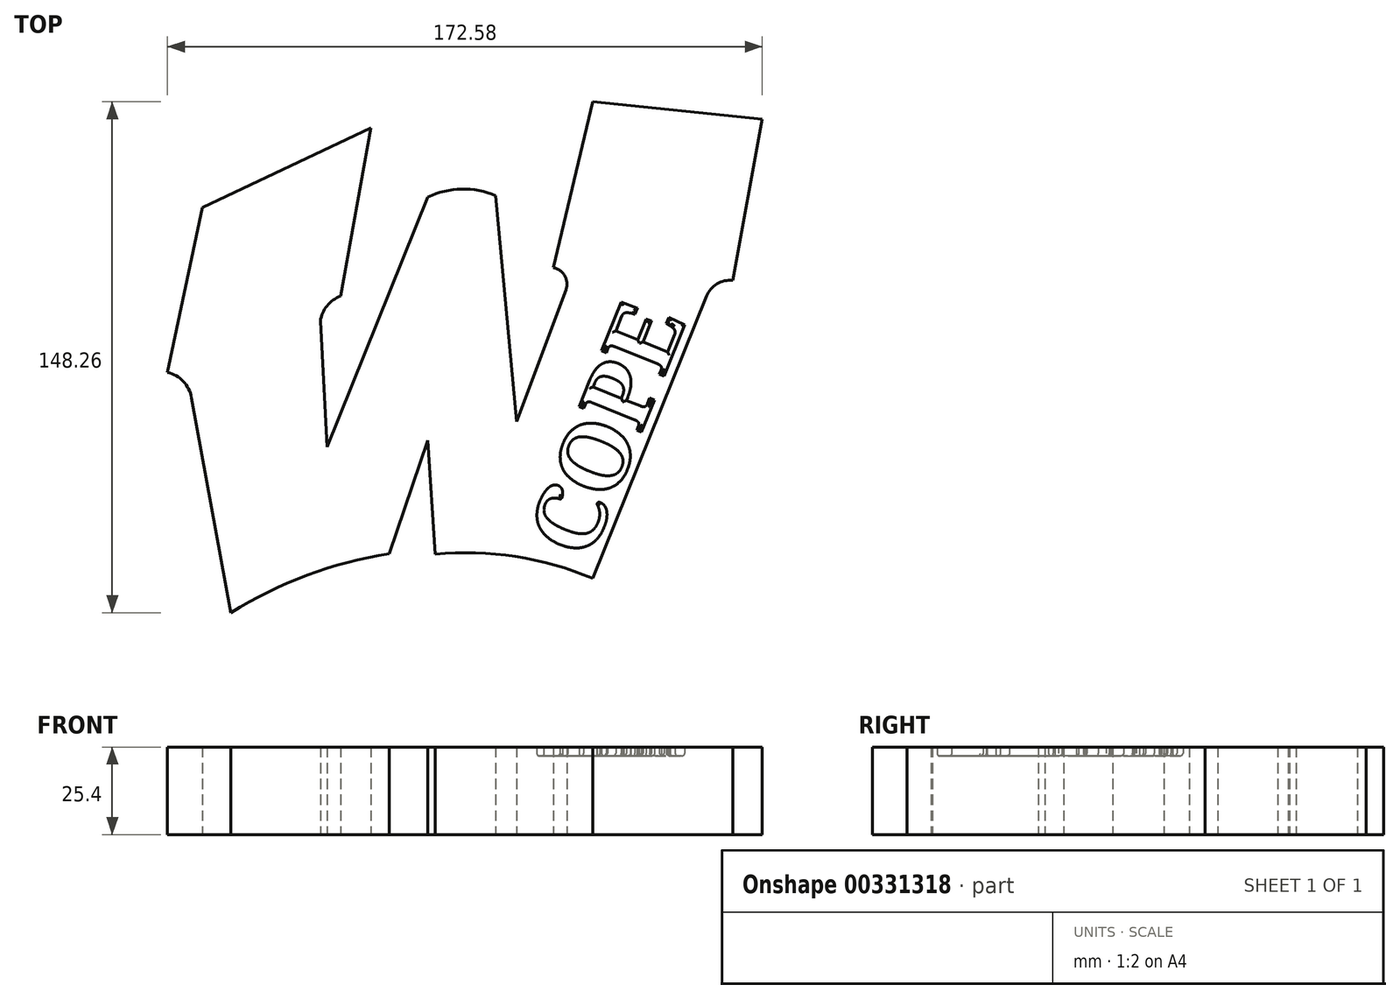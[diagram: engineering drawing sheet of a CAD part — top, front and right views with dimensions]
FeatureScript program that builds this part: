
annotation { "Feature Type Name" : "Feature", "Feature Type Description" : "" }
export const myFeature = defineFeature(function(context is Context, id is Id, definition is map)
    precondition{}
    {
        {
            var Q0;
            Q0=qCreatedBy(makeId("Top.planeOp"),FACE);
            var sketch = newSketch(context, id + "F0", { "sketchPlane" : qUnion([Q0])});
            skLineSegment(sketch, "E0", {"start": v(-75.92, 43.74) * mm, "end": v(-27.1, 66.86) * mm});
            skLineSegment(sketch, "E1", {"start": v(-27.1, 66.86) * mm, "end": v(-35.87, 18.03) * mm});
            skLineSegment(sketch, "E2", {"start": v(-41.74, 10.74) * mm, "end": v(-39.73, -25.7) * mm});
            skLineSegment(sketch, "E3", {"start": v(-39.73, -25.7) * mm, "end": v(-10.52, 46.77) * mm});
            skLineSegment(sketch, "E4", {"start": v(9.14, 47.22) * mm, "end": v(15.27, -18.34) * mm});
            skLineSegment(sketch, "E5", {"start": v(15.27, -18.34) * mm, "end": v(29.5, 19.85) * mm});
            skLineSegment(sketch, "E6", {"start": v(25.93, 26.33) * mm, "end": v(37.26, 74.43) * mm});
            skLineSegment(sketch, "E7", {"start": v(37.26, 74.43) * mm, "end": v(86.49, 69.45) * mm});
            skLineSegment(sketch, "E8", {"start": v(86.49, 69.45) * mm, "end": v(77.92, 22.62) * mm});
            skLineSegment(sketch, "E9", {"start": v(70.35, 18.03) * mm, "end": v(37.26, -63.87) * mm});
            skLineSegment(sketch, "E10", {"start": v(-8.37, -56.9) * mm, "end": v(-10.52, -23.8) * mm});
            skLineSegment(sketch, "E11", {"start": v(-10.52, -23.8) * mm, "end": v(-21.72, -56.7) * mm});
            skLineSegment(sketch, "E12", {"start": v(-67.75, -73.83) * mm, "end": v(-79.11, -11.46) * mm});
            skLineSegment(sketch, "E13", {"start": v(-86.09, -4.09) * mm, "end": v(-75.92, 43.74) * mm});
            skArc(sketch, "E14", {"start": v(9.14, 47.22) * mm, "mid": v(-0.74, 49.12) * mm, "end": v(-10.52, 46.77) * mm});
            skArc(sketch, "E15", {"start": v(29.5, 19.85) * mm, "mid": v(29.2, 23.9) * mm, "end": v(25.93, 26.33) * mm});
            skArc(sketch, "E16", {"start": v(77.92, 22.62) * mm, "mid": v(73.37, 21.59) * mm, "end": v(70.35, 18.03) * mm});
            skArc(sketch, "E17", {"start": v(-35.87, 18.03) * mm, "mid": v(-39.83, 15.2) * mm, "end": v(-41.74, 10.74) * mm});
            skArc(sketch, "E18", {"start": v(-79.11, -11.46) * mm, "mid": v(-81.5, -6.74) * mm, "end": v(-86.09, -4.09) * mm});
            skArc(sketch, "E19", {"start": v(-21.72, -56.7) * mm, "mid": v(-45.59, -62.98) * mm, "end": v(-67.75, -73.83) * mm});
            skArc(sketch, "E20", {"start": v(37.26, -63.87) * mm, "mid": v(14.88, -57.55) * mm, "end": v(-8.37, -56.9) * mm});
            skSolve(sketch);
        }
        {
            var Q0;
            Q0=qCreatedBy(makeId("Top.planeOp"),FACE);
            var sketch = newSketch(context, id + "F1", { "sketchPlane" : qUnion([Q0])});
            skText(sketch, "E21", { "text": "COPE", "fontName": "NotoSerif-Bold.ttf"});
            skLineSegment(sketch, "E22", {"start": v(45.56, -52.33) * mm, "end": v(64.67, -4.96) * mm});
            const initialGuessF1  = {"E21": [0.03626, -0.0591, 0.37408, 0.9274, 0.01974]};
            skSetInitialGuess(sketch, initialGuessF1);
            skSolve(sketch);
        }
        {
            var Q0;
            Q0=makeQuery(id+"F0.imprint","IMPRINT",FACE,{"disambiguationData":[TD([[makeQuery(id+"F0.imprint","IMPRINT",EDGE,{"derivedFrom":sQuery(id+"F0.wireOp",EDGE,"E0")}),-1.0]])]});
            extrude(context, id + "F2", {"entities" : qUnion([Q0]), "depth" : 25.4 * mm});
        }
        {
            var Q0;
            Q0=makeQuery(id+"F1.imprint","IMPRINT",FACE,{"disambiguationData":[TD([[makeQuery(id+"F1.imprint","IMPRINT",EDGE,{"derivedFrom":sQuery(id+"F1.wireOp",EDGE,"E21.sketch_text.stroke-0")}),-1.0]])]});
            var Q1;
            Q1=makeQuery(id+"F1.imprint","IMPRINT",FACE,{"disambiguationData":[TD([[makeQuery(id+"F1.imprint","IMPRINT",EDGE,{"derivedFrom":sQuery(id+"F1.wireOp",EDGE,"E21.sketch_text.stroke-112")}),-1.0]])]});
            var Q2;
            Q2=makeQuery(id+"F1.imprint","IMPRINT",FACE,{"disambiguationData":[TD([[makeQuery(id+"F1.imprint","IMPRINT",EDGE,{"derivedFrom":sQuery(id+"F1.wireOp",EDGE,"E21.sketch_text.stroke-38")}),-1.0]])]});
            var Q3;
            Q3=makeQuery(id+"F1.imprint","IMPRINT",FACE,{"disambiguationData":[TD([[makeQuery(id+"F1.imprint","IMPRINT",EDGE,{"derivedFrom":sQuery(id+"F1.wireOp",EDGE,"E21.sketch_text.stroke-70")}),-1.0]])]});
            var Q4;
            Q4 = qSketchRegion(id + "F1", true);
            extrude(context, id + "F3", {"entities" : qUnion([Q0, Q1, Q2, Q3, Q4]), "operationType" : NewBodyOperationType.REMOVE, "depth" : 25.4 * mm, "hasSecondDirection" : true, "secondDirectionOppositeDirection" : false, "secondDirectionDepth" : 22.86 * mm});
        }
        {
            var Q0;
            Q0=makeQuery(id+"F3.boolean.opBoolean","COPY",EDGE,{"derivedFrom":makeQuery(id+"F3.opExtrude","CAP_EDGE",EDGE,{"disambiguationData":[OSD([sQuery(id+"F1.wireOp",EDGE,"E21.sketch_text.stroke-53")])],"isStart":true})});
            var Q1;
            Q1=makeQuery(id+"F3.boolean.opBoolean","COPY",EDGE,{"derivedFrom":makeQuery(id+"F3.opExtrude","CAP_EDGE",EDGE,{"disambiguationData":[OSD([sQuery(id+"F1.wireOp",EDGE,"E21.sketch_text.stroke-111")])],"isStart":true})});
            var Q2;
            Q2=makeQuery(id+"F3.boolean.opBoolean","COPY",EDGE,{"derivedFrom":makeQuery(id+"F3.opExtrude","CAP_EDGE",EDGE,{"disambiguationData":[OSD([sQuery(id+"F1.wireOp",EDGE,"E21.sketch_text.stroke-100")])],"isStart":true})});
            var Q3;
            Q3=makeQuery(id+"F3.boolean.opBoolean","COPY",EDGE,{"derivedFrom":makeQuery(id+"F3.opExtrude","CAP_EDGE",EDGE,{"disambiguationData":[OSD([sQuery(id+"F1.wireOp",EDGE,"E21.sketch_text.stroke-75")])],"isStart":true})});
            var Q4;
            Q4=makeQuery(id+"F3.boolean.opBoolean","COPY",EDGE,{"derivedFrom":makeQuery(id+"F3.opExtrude","CAP_EDGE",EDGE,{"disambiguationData":[OSD([sQuery(id+"F1.wireOp",EDGE,"E21.sketch_text.stroke-82")])],"isStart":true})});
            var Q5;
            Q5=makeQuery(id+"F3.boolean.opBoolean","COPY",EDGE,{"derivedFrom":makeQuery(id+"F3.opExtrude","CAP_EDGE",EDGE,{"disambiguationData":[OSD([sQuery(id+"F1.wireOp",EDGE,"E21.sketch_text.stroke-85")])],"isStart":true})});
            var Q6;
            Q6=makeQuery(id+"F3.boolean.opBoolean","COPY",EDGE,{"derivedFrom":makeQuery(id+"F3.opExtrude","CAP_EDGE",EDGE,{"disambiguationData":[OSD([sQuery(id+"F1.wireOp",EDGE,"E21.sketch_text.stroke-105")])],"isStart":true})});
            var Q7;
            Q7=makeQuery(id+"F3.boolean.opBoolean","COPY",EDGE,{"derivedFrom":makeQuery(id+"F3.opExtrude","CAP_EDGE",EDGE,{"disambiguationData":[OSD([sQuery(id+"F1.wireOp",EDGE,"E21.sketch_text.stroke-141")])],"isStart":true})});
            var Q8;
            Q8=makeQuery(id+"F3.boolean.opBoolean","COPY",EDGE,{"derivedFrom":makeQuery(id+"F3.opExtrude","CAP_EDGE",EDGE,{"disambiguationData":[OSD([sQuery(id+"F1.wireOp",EDGE,"E21.sketch_text.stroke-142")])],"isStart":true})});
            var Q9;
            Q9=makeQuery(id+"F3.boolean.opBoolean","COPY",EDGE,{"derivedFrom":makeQuery(id+"F3.opExtrude","CAP_EDGE",EDGE,{"disambiguationData":[OSD([sQuery(id+"F1.wireOp",EDGE,"E21.sketch_text.stroke-145")])],"isStart":true})});
            var Q10;
            Q10=makeQuery(id+"F3.boolean.opBoolean","COPY",EDGE,{"derivedFrom":makeQuery(id+"F3.opExtrude","CAP_EDGE",EDGE,{"disambiguationData":[OSD([sQuery(id+"F1.wireOp",EDGE,"E21.sketch_text.stroke-144")])],"isStart":true})});
            var Q11;
            Q11=makeQuery(id+"F3.boolean.opBoolean","COPY",EDGE,{"derivedFrom":makeQuery(id+"F3.opExtrude","CAP_EDGE",EDGE,{"disambiguationData":[OSD([sQuery(id+"F1.wireOp",EDGE,"E21.sketch_text.stroke-140")])],"isStart":true})});
            var Q12;
            Q12=makeQuery(id+"F3.boolean.opBoolean","COPY",EDGE,{"derivedFrom":makeQuery(id+"F3.opExtrude","CAP_EDGE",EDGE,{"disambiguationData":[OSD([sQuery(id+"F1.wireOp",EDGE,"E21.sketch_text.stroke-136")])],"isStart":true})});
            var Q13;
            Q13=makeQuery(id+"F3.boolean.opBoolean","COPY",EDGE,{"derivedFrom":makeQuery(id+"F3.opExtrude","CAP_EDGE",EDGE,{"disambiguationData":[OSD([sQuery(id+"F1.wireOp",EDGE,"E21.sketch_text.stroke-135")])],"isStart":true})});
            var Q14;
            Q14=makeQuery(id+"F3.boolean.opBoolean","COPY",EDGE,{"derivedFrom":makeQuery(id+"F3.opExtrude","CAP_EDGE",EDGE,{"disambiguationData":[OSD([sQuery(id+"F1.wireOp",EDGE,"E21.sketch_text.stroke-134")])],"isStart":true})});
            var Q15;
            Q15=makeQuery(id+"F3.boolean.opBoolean","COPY",EDGE,{"derivedFrom":makeQuery(id+"F3.opExtrude","CAP_EDGE",EDGE,{"disambiguationData":[OSD([sQuery(id+"F1.wireOp",EDGE,"E21.sketch_text.stroke-133")])],"isStart":true})});
            var Q16;
            Q16=makeQuery(id+"F3.boolean.opBoolean","COPY",EDGE,{"derivedFrom":makeQuery(id+"F3.opExtrude","CAP_EDGE",EDGE,{"disambiguationData":[OSD([sQuery(id+"F1.wireOp",EDGE,"E21.sketch_text.stroke-128")])],"isStart":true})});
            var Q17;
            Q17=makeQuery(id+"F3.boolean.opBoolean","COPY",EDGE,{"derivedFrom":makeQuery(id+"F3.opExtrude","CAP_EDGE",EDGE,{"disambiguationData":[OSD([sQuery(id+"F1.wireOp",EDGE,"E21.sketch_text.stroke-121")])],"isStart":true})});
            var Q18;
            Q18=makeQuery(id+"F3.boolean.opBoolean","COPY",EDGE,{"derivedFrom":makeQuery(id+"F3.opExtrude","CAP_EDGE",EDGE,{"disambiguationData":[OSD([sQuery(id+"F1.wireOp",EDGE,"E21.sketch_text.stroke-114")])],"isStart":true})});
            var Q19;
            Q19=makeQuery(id+"F3.boolean.opBoolean","COPY",EDGE,{"derivedFrom":makeQuery(id+"F3.opExtrude","CAP_EDGE",EDGE,{"disambiguationData":[OSD([sQuery(id+"F1.wireOp",EDGE,"E21.sketch_text.stroke-62")])],"isStart":true})});
            var Q20;
            Q20=makeQuery(id+"F3.boolean.opBoolean","COPY",EDGE,{"derivedFrom":makeQuery(id+"F3.opExtrude","CAP_EDGE",EDGE,{"disambiguationData":[OSD([sQuery(id+"F1.wireOp",EDGE,"E21.sketch_text.stroke-120")])],"isStart":true})});
            var Q21;
            Q21=makeQuery(id+"F3.boolean.opBoolean","COPY",EDGE,{"derivedFrom":makeQuery(id+"F3.opExtrude","CAP_EDGE",EDGE,{"disambiguationData":[OSD([sQuery(id+"F1.wireOp",EDGE,"E21.sketch_text.stroke-119")])],"isStart":true})});
            var Q22;
            Q22=makeQuery(id+"F3.boolean.opBoolean","COPY",EDGE,{"derivedFrom":makeQuery(id+"F3.opExtrude","CAP_EDGE",EDGE,{"disambiguationData":[OSD([sQuery(id+"F1.wireOp",EDGE,"E21.sketch_text.stroke-118")])],"isStart":true})});
            var Q23;
            Q23=makeQuery(id+"F3.boolean.opBoolean","COPY",EDGE,{"derivedFrom":makeQuery(id+"F3.opExtrude","CAP_EDGE",EDGE,{"disambiguationData":[OSD([sQuery(id+"F1.wireOp",EDGE,"E21.sketch_text.stroke-143")])],"isStart":true})});
            fillet(context, id + "F4", {"entities" : qUnion([Q0, Q1, Q2, Q3, Q4, Q5, Q6, Q7, Q8, Q9, Q10, Q11, Q12, Q13, Q14, Q15, Q16, Q17, Q18, Q19, Q20, Q21, Q22, Q23]), "radius" : 0.76 * mm, "tangentPropagation" : true, "allowEdgeOverflow" : false});
        }
        {
            var Q0;
            Q0=makeQuery(id+"F3.boolean.opBoolean","COPY",EDGE,{"derivedFrom":makeQuery(id+"F3.opExtrude","CAP_EDGE",EDGE,{"disambiguationData":[OSD([sQuery(id+"F1.wireOp",EDGE,"E21.sketch_text.stroke-15")])],"isStart":true})});
            var Q1;
            Q1=makeQuery(id+"F3.boolean.opBoolean","COPY",EDGE,{"derivedFrom":makeQuery(id+"F3.opExtrude","CAP_EDGE",EDGE,{"disambiguationData":[OSD([sQuery(id+"F1.wireOp",EDGE,"E21.sketch_text.stroke-16")])],"isStart":true})});
            fillet(context, id + "F5", {"entities" : qUnion([Q0, Q1]), "radius" : 0.64 * mm, "tangentPropagation" : true, "allowEdgeOverflow" : false});
        }
        {
            var Q0;
            Q0=makeQuery(id+"F3.boolean.opBoolean","COPY",EDGE,{"derivedFrom":makeQuery(id+"F3.opExtrude","CAP_EDGE",EDGE,{"disambiguationData":[OSD([sQuery(id+"F1.wireOp",EDGE,"E21.sketch_text.stroke-33")])],"isStart":true})});
            fillet(context, id + "F6", {"entities" : qUnion([Q0]), "radius" : 0.5 * mm, "tangentPropagation" : true, "allowEdgeOverflow" : false});
        }
    });
